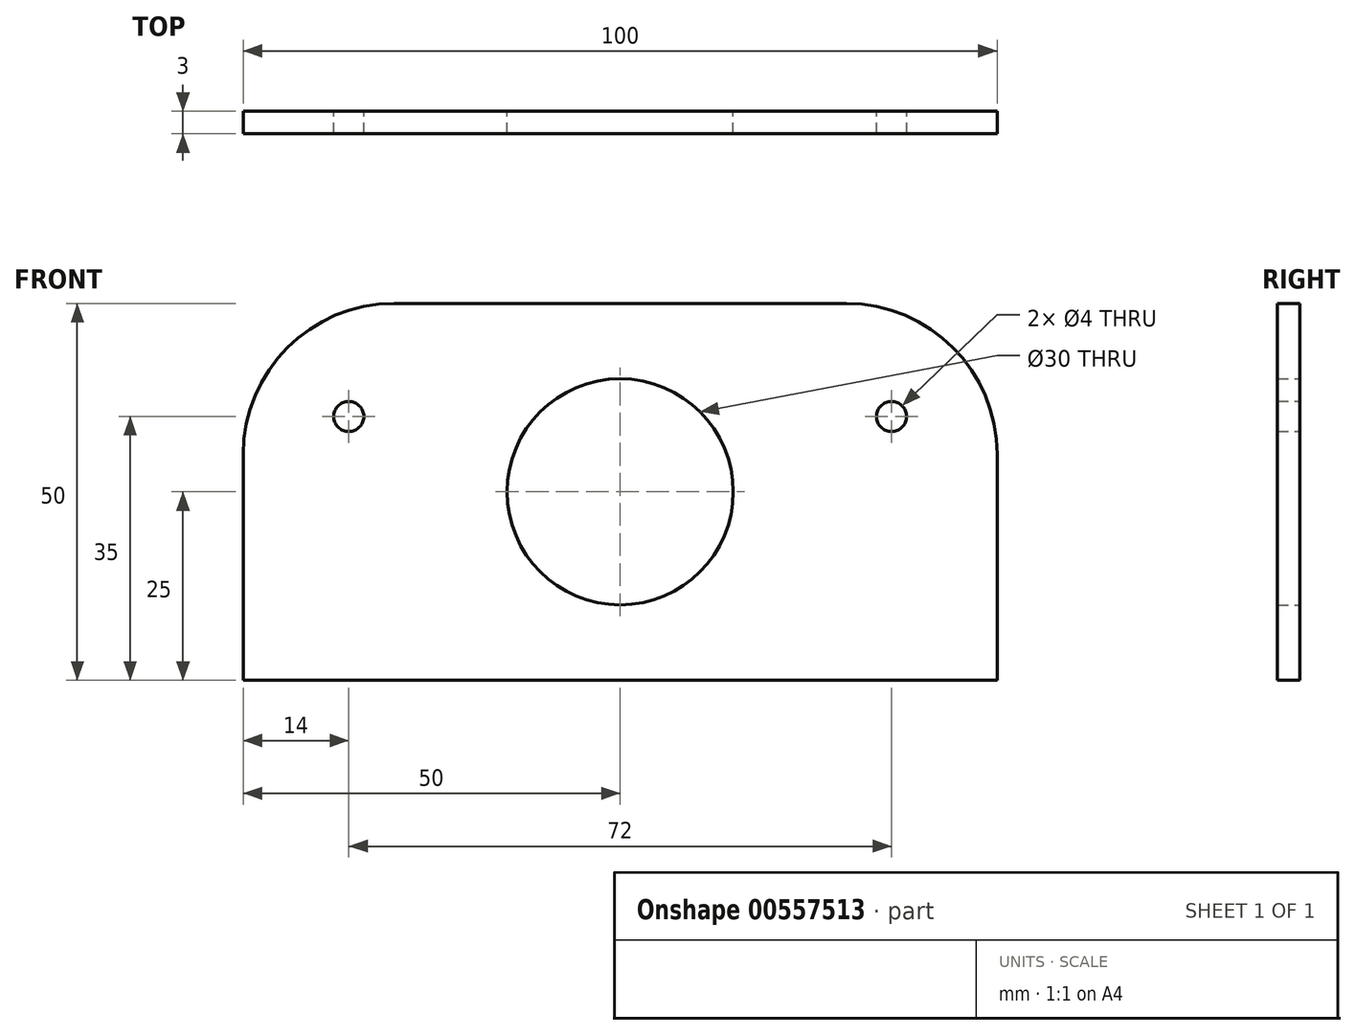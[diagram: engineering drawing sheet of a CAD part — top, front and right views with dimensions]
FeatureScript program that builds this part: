
annotation { "Feature Type Name" : "Feature", "Feature Type Description" : "" }
export const myFeature = defineFeature(function(context is Context, id is Id, definition is map)
    precondition{}
    {
        {
            var Q0;
            Q0=qCreatedBy(makeId("Front.planeOp"),FACE);
            var sketch = newSketch(context, id + "F0", { "sketchPlane" : qUnion([Q0])});
            skLineSegment(sketch, "E0.bottom", {"start": v(-50, 25) * mm, "end": v(50, 25) * mm});
            skLineSegment(sketch, "E0.top", {"start": v(-50, -25) * mm, "end": v(50, -25) * mm});
            skLineSegment(sketch, "E0.left", {"start": v(-50, 25) * mm, "end": v(-50, -25) * mm});
            skLineSegment(sketch, "E0.right", {"start": v(50, 25) * mm, "end": v(50, -25) * mm});
            skPoint(sketch, "E0.middle", {"position": v(0, 0) * mm});
            skCircle(sketch, "E1", {"center": v(0, 0) * mm, "radius": 15 * mm});
            skCircle(sketch, "E2", {"center": v(-36, 10) * mm, "radius": 2 * mm});
            skCircle(sketch, "E3", {"center": v(36, 10) * mm, "radius": 2 * mm});
            skSolve(sketch);
        }
        {
            var Q0;
            Q0=makeQuery(id+"F0.imprint","IMPRINT",FACE,{"disambiguationData":[TD([[makeQuery(id+"F0.imprint","IMPRINT",EDGE,{"derivedFrom":sQuery(id+"F0.wireOp",EDGE,"E0.bottom")}),-1.0]])]});
            extrude(context, id + "F1", {"entities" : qUnion([Q0]), "depth" : 3 * mm, "offsetDistance" : 25 * mm});
        }
        {
            var Q0;
            Q0=makeQuery(id+"F1.opExtrude","SWEPT_EDGE",EDGE,{"disambiguationData":[OSD([sQuery(id+"F0.wireOp",EDGE,"E0.bottom"),sQuery(id+"F0.wireOp",EDGE,"E0.left")])]});
            var Q1;
            Q1=makeQuery(id+"F1.opExtrude","SWEPT_EDGE",EDGE,{"disambiguationData":[OSD([sQuery(id+"F0.wireOp",EDGE,"E0.bottom"),sQuery(id+"F0.wireOp",EDGE,"E0.right")])]});
            fillet(context, id + "F2", {"entities" : qUnion([Q0, Q1]), "radius" : 20 * mm, "tangentPropagation" : true, "allowEdgeOverflow" : false});
        }
    });
